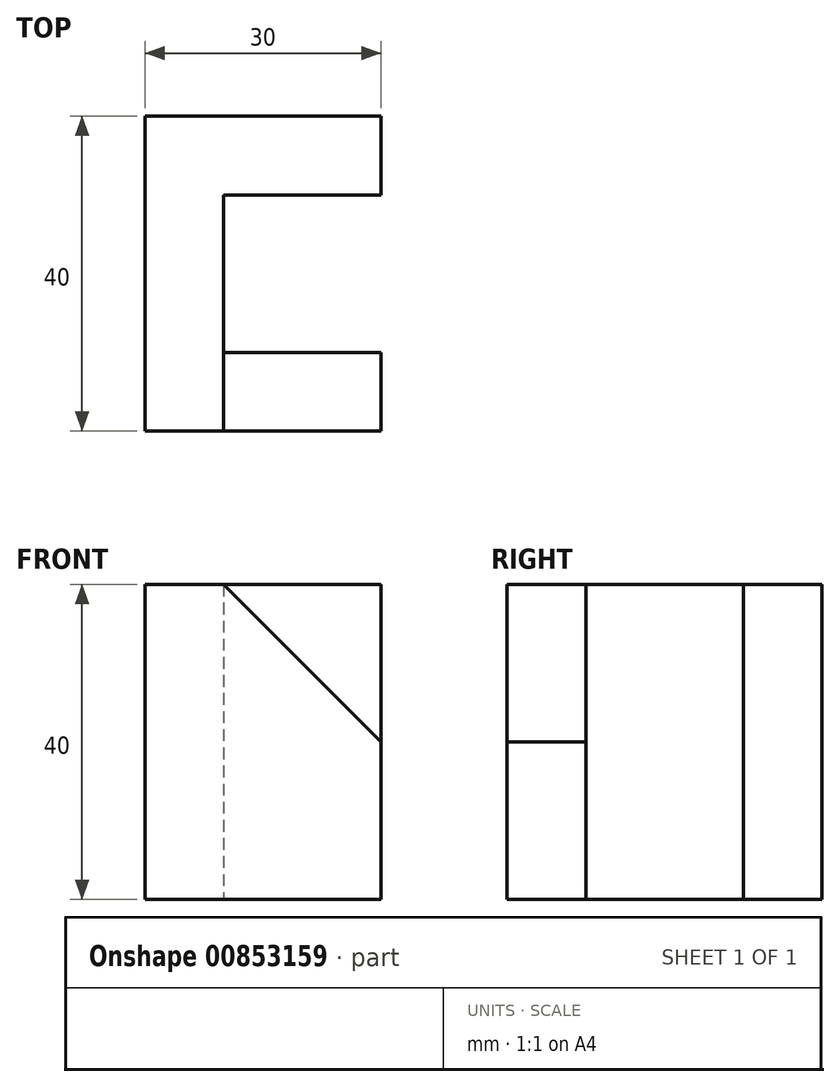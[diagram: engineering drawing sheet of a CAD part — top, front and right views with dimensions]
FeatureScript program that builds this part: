
annotation { "Feature Type Name" : "Feature", "Feature Type Description" : "" }
export const myFeature = defineFeature(function(context is Context, id is Id, definition is map)
    precondition{}
    {
        {
            var Q0;
            Q0=qCreatedBy(makeId("Top.planeOp"),FACE);
            var sketch = newSketch(context, id + "F0", { "sketchPlane" : qUnion([Q0])});
            skLineSegment(sketch, "E0.bottom", {"start": v(-50, 20) * mm, "end": v(15, 20) * mm});
            skLineSegment(sketch, "E0.top", {"start": v(-50, -20) * mm, "end": v(15, -20) * mm});
            skLineSegment(sketch, "E0.left", {"start": v(-50, 20) * mm, "end": v(-50, -20) * mm});
            skLineSegment(sketch, "E0.right", {"start": v(20, 15) * mm, "end": v(20, -15) * mm});
            skCircle(sketch, "E1", {"center": v(0, 0) * mm, "radius": 10 * mm});
            skLineSegment(sketch, "E2.bottom", {"start": v(-50, 20) * mm, "end": v(-40, 20) * mm});
            skLineSegment(sketch, "E2.top", {"start": v(-50, -20) * mm, "end": v(-40, -20) * mm});
            skLineSegment(sketch, "E2.right", {"start": v(-40, 10) * mm, "end": v(-40, -10) * mm});
            skLineSegment(sketch, "E3.bottom", {"start": v(-50, 20) * mm, "end": v(-20, 20) * mm});
            skLineSegment(sketch, "E3.top", {"start": v(-40, 10) * mm, "end": v(-20, 10) * mm});
            skLineSegment(sketch, "E3.left", {"start": v(-50, 20) * mm, "end": v(-50, 10) * mm});
            skLineSegment(sketch, "E3.right", {"start": v(-20, 20) * mm, "end": v(-20, 10) * mm});
            skLineSegment(sketch, "E4.bottom", {"start": v(-50, -20) * mm, "end": v(-20, -20) * mm});
            skLineSegment(sketch, "E4.top", {"start": v(-40, -10) * mm, "end": v(-20, -10) * mm});
            skLineSegment(sketch, "E4.left", {"start": v(-50, -20) * mm, "end": v(-50, -10) * mm});
            skLineSegment(sketch, "E4.right", {"start": v(-20, -20) * mm, "end": v(-20, -10) * mm});
            skArc(sketch, "E5", {"start": v(20, 15) * mm, "mid": v(18.54, 18.54) * mm, "end": v(15, 20) * mm});
            skArc(sketch, "E6", {"start": v(15, -20) * mm, "mid": v(18.54, -18.54) * mm, "end": v(20, -15) * mm});
            skPoint(sketch, "E7.orphan", {"position": v(20, 20) * mm});
            skPoint(sketch, "E8.orphan", {"position": v(20, -20) * mm});
            skSolve(sketch);
        }
        {
            var Q0;
            Q0=makeQuery(id+"F0.imprint","IMPRINT",FACE,{"disambiguationData":[TD([[makeQuery(id+"F0.imprint","IMPRINT",EDGE,{"derivedFrom":sQuery(id+"F0.wireOp",EDGE,"E0.bottom")}),-1.0]])]});
            extrude(context, id + "F1", {"entities" : qUnion([Q0]), "depth" : 20 * mm, "offsetDistance" : 25 * mm});
        }
        {
            var Q0;
            Q0=makeQuery(id+"F0.imprint","IMPRINT",FACE,{"disambiguationData":[TD([[makeQuery(id+"F0.imprint","IMPRINT",EDGE,{"derivedFrom":sQuery(id+"F0.wireOp",EDGE,"E0.left")}),1.0]])]});
            extrude(context, id + "F2", {"entities" : qUnion([Q0]), "operationType" : NewBodyOperationType.ADD, "depth" : 40 * mm, "offsetDistance" : 25 * mm});
        }
        {
            var Q0;
            Q0=makeQuery(id+"F2.opExtrude","CAP_EDGE",EDGE,{"disambiguationData":[OSD([sQuery(id+"F0.wireOp",EDGE,"E4.right")])],"isStart":false});
            chamfer(context, id + "F3", {"entities" : qUnion([Q0]), "width" : 20 * mm, "tangentPropagation" : true});
        }
    });
